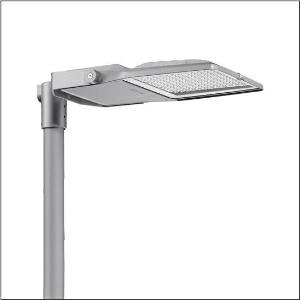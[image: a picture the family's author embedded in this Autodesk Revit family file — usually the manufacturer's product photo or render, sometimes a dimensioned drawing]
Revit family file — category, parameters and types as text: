
# Revit family: floodlight_fl_21_iq_midi___pl43_5xa7781f2a3a_7a49
name_source: partatom
category: Lighting Fixtures
units: mm (PartAtom-declared; Revit-internal decimal feet)

## family parameters
Cut with Voids When Loaded = No
Host = Face
Light Source = No
Part Type = Normal
Room Calculation Point = No
Round Connector Dimension = Use Diameter
Shared = No

## types (1)
- --- (1 x LED, 36680 lm, 270.2 W, 3000K)
    Apparent Load = 270 VA
    CIE Flux Codes = 27 78 99 100 100
    Color Rendering = 70
    Color Temperature = 3000K
    Default Elevation = 1800 mm
    Description = Floodlight FL 21 iQ midi, floodlight, primary light control with lens, of PMMA, primary optical cover: protective disc, of toughened safety glass, transparent, light distribution: PL43, light emission: direct distribution, installation type: surface-mounted, lamps: LED, High Power LED, rated values: 36.680lm | 270,2W | 135,8lm/W (begin service life); end service life: 36.680lm | 286,6W; at 50% lumin. flux: 18.340lm | 117,4W | 156,2lm/W, colour temperature: 3000K, colour rendering: CRI > 70, light colour: 730, light setting 1 begin service life: 100% | 36.680lm | 270,2W | 135,8lm/W | 3.000K, light setting 1 end service life: 286,6W, further light settings possible, control: optimised constant luminous flux control (CLO 2.0), Desk-Remote (wireless, voltage-free reading and setting of iQ features in the workshop via application-optimized NFC function/RFID function), Light-Fading, Smart-Wire, Night-Set, Lumen-Switch, Temp-Guard, Auto-Match, pre-setting: linear dimming characteristic, with terminal, 6-pole, mains connection: 220..240V, AC, 50/60Hz, luminaire housing, of diecast aluminium, powder-coated, SITECO metallic grey (DB 702S), corrosivity category C5 mid according to DIN EN ISO 12944suitable for swimming poolschlorine-resistant, sealing non-destructively replaceable, please order mast flange separately, mast bracket, of steel, galvanised, powder-coated, SITECO metallic grey (DB 702S), protection rating (complete): IP66, insulation class (complete): insulation class II (safety insulation), certification: CE, ENEC, VDE, protection symbol: D, impact resistance: IK08, permissible operating ambient temperature: -40..+40°C, permissible operating ambient temperature for outdoor applications: -40..+50°C, standard: DIN EN 12944, LABS conformity tested according to VDMA 24364:2018-05, packaging unit: 1 piece

Light Distribution: PL43
    Height = 76 mm
    Lamp = 1 x LED
    Lamp Light Flux = 36680 lm
    Lamp Power = 270.2 W
    Lamp count = 1
    Length = 657 mm
    Luminous efficacy = 136 lm/W
    Manufacturer = Siteco
    ModVariant = No
    Model = 5XA7781F2A3A
    Mounting Place = Pole
    Mounting Type = Pole annexe
    Number of Poles = 1
    OnlyDefault = Yes
    Power Factor = 1
    Product Name = Floodlight FL 21 iQ midi | PL43
    Product group = floodlight | pylon annexe
    ProductGroupID = 6201
    Protection Class = Protection class II
    Protection Degree = IP 66
    RLX_Detail_Level = 1
    RLX_Emergency_Light_Flux = 0 lm
    RLX_Emergency_Type = 0
    RLX_Emergency_Type_DB = No
    RlxData = <blob elided: 154257 chars, md5=0e1dd3ab>
    Socket = socket
    Standby Power = 0 W
    System Light Flux = 36680 lm
    System Power = 270 W
    Type Comments = factory setting: luminous flux: 100 % | dim-lin: 254 | 620 mA
    Type Image = l_1007123.jpg
    URL = http://relux.com
    VarID = @adj_106389
    Voltage = 0 V
    Weight = 0.00 kg
    Width = 442 mm

## geometry (parser evidence)
native form markers: Blend x4, Sweep x13
no freeform markers — native parametric forms only
